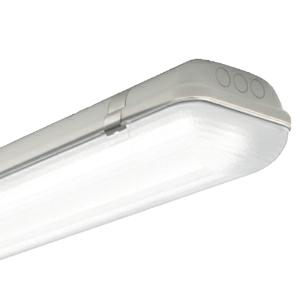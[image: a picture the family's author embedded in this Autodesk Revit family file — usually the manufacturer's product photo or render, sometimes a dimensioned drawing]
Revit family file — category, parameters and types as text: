
# Revit family: 3f_filippi_-_3f_linda_soft_3f_filippi_-_58732_-_3f_linda_led_soft_2x12w_l660
name_source: partatom
category: Lighting Fixtures
units: mm (PartAtom-declared; Revit-internal decimal feet)

## family parameters
Cut with Voids When Loaded = No
Host = Face
Light Source = No
Part Type = Normal
Room Calculation Point = No
Round Connector Dimension = Use Diameter
Shared = No

## types (1)
- 3F Filippi - 3F Linda Soft (1 x LED, 3578 lm, 28 W, 4000 K)
    Apparent Load = 28 VA
    Approval mark = CE
    CIE Flux Codes = 42 72 91 93 100
    Color Rendering = 80
    Color Temperature = 4000 K
    Control Gear = Electronic ballast
    Default Elevation = 1800 mm
    Description = ILLUMINOTECHNICAL
Luminous efficiency 100% (DLOR 93%, ULOR 7%).
Initial luminous flux of the luminaire 3578 lm.
Direct symmetric distribution.
Installation Interdistance Transv.D = 1.35 x hu - Long.D = 1.24 x hu.
Tabular UGR (CIE 117 - 4H-8H; S=0.25H; 70/50/20): RUG 24.4 - 22.3.
Beam angle: 131° - 111°.
Luminous efficacy 128 lm/W.
Lifetime (L93/B10): 30000 h. (tq+25°C)
Lifetime (L90/B10): 50000 h. (tq+25°C)
Lifetime (L85/B10): 80000 h. (tq+25°C)
Lifetime (L80/B10): 100000 h. (tq+25°C)
Lifetime (L85/B10): 50000 h. (tq+35°C)
Sudden decreased luminous flux after 50000 hours: 0% (C0).
Photobiological safety in compliance with IEC/TR 62778: RG0 risk exempt, (IEC 62471).
In compliance with IEC/EN 62722-2-1 - IEC/EN 62717 standards.

SOURCE
2 linear LED modules 12W/840.
Energy efficiency class (UE 2019/2020 - UE 2019/2015): D.
CIE 13.3 Colour rendering index: CRI >80 (R9 <50%).
IES TM-30 Fidelity Index: Rf = 84 Rg = 95.
CCT nominal colour temperature 4000 K.
Colour initial tolerance (MacAdam): SDCM 3.

MECHANICAL
Self-extinguishing V2 polycarbonate housing, injection moulded, RAL 7035 grey.
Ecologic anti-aging injected sealing gasket.
Soft opal diffuser in self-extinguishing V2 polycarbonate, photo-engraved interior, UV stabilised, injection moulded.
Gear-holder reflector in hot-dip galvanised steel, painted with white polyester base.
Snug fit safety snap-lock clips for diffuser mounting in stainless steel, screwdriver opening.
Fixing brackets in stainless steel.
Possibility for technicians to access the interior of the luminaire.
Luminaire with limited surface temperature. - D - (EN 60598-2-24)
Dimensions: 660x160 mm, height 100 mm. Weight 1.65 kg.
IP66 protection degree.
Mechanical strength to impacts IK10 (20 joule).
Glow-wire test resistance 850°C.

ELECTRICAL
Halogen Free electronic wiring 230V-50/60Hz, power factor 0.90, THD <25%, constant output current, SELV, class I, 1 driver.
Power of the luminaire 28 W.
ENEC - CE.
SAFE FLICKER: PstLM=<1 and SVM=<0.4 (IEC TR 61547-1 and IEC TR 63158), to ensure a more comfortable and safe light.
Luminaire compliant with EN 60598-2-22 for power supply from a centralised emergency system CPSS (Central Power Supply System), not incorporated in the luminaire - high risk areas excluded. The default power and flux are 100% in AC and 100% in DC.
Ambient temperature from -20°C to +35°C.
Temperature class T6 max 85°C.
Relative humidity UR: <85%.

INSTALLATION
Ceiling / Suspended / Wall.
All accessories dedicated to this product are available on the Catalog and on our website www.3F-Filippi.com.

APPLICATIONS
Suitable product for food production plants (HACCP), IFS (Food Version 6), BRC (GSFS Food Version 7).
Dry, dusty indoor environments, subject to occasional water splashes.
Luminaires designed for diffuse direct/indirect lighting suitable to provide optimum visual comfort.
Transit areas, stairwells.
Virtually shatterproof polycarbonate compatibly with the fumes / atmospheres that compromise the elasticity of plastic materials.
Suitable for illumination of public car parks and parking grounds referred to DIN 67528:2018-04.

WARNING
Fixture not suitable for cold stores with an ambient temperature <0°C and/or relative humidity >85%.
Luminaire designed for disposal/recycling at end-of-life.
Replaceable (LED only) light source by a professional. Replaceable control gear by a professional.
    Height = 100 mm  [stored 0.328084 ft]
    Lamp = 1 x LED
    Lamp Light Flux = 3578 lm
    Lamp Power = 28 W
    Lamp count = 1
    Length = 660 mm
    Lifetime = 50000 h
    Luminous efficacy = 128 lm/W
    Manufacturer = 3F Filippi
    ModVariant = No
    Model = 3F Filippi - 58732 - 3F Linda LED Soft 2x12W L660
    Mounting Place = Ceiling
    Mounting Type = Pendant
    Number of Poles = 1
    OnlyDefault = Yes
    Power Factor = 1
    Product Name = 3F Filippi - 3F Linda Soft
    Product group = pendant luminaire
    ProductGroupID = 9
    Protection Class = Protection class I
    Protection Degree = IP 66
    RLX_Detail_Level = 1
    RLX_Emergency_Light_Flux = 0 lm
    RLX_Emergency_Type = 0
    RLX_Emergency_Type_DB = No
    RlxData = <blob elided: 69265 chars, md5=5b45bd41>
    Socket = socket
    Standby Power = 0 W
    System Light Flux = 3578 lm
    System Power = 28 W
    Type Comments = Product without accessories
    Type Image = 3ffilippi_3f_linda_led_soft_2x.jpg
    URL = http://relux.com
    VarID = ---
    Voltage = 0 V
    Weight = 0.00 kg
    Width = 160 mm

note: [stored X ft] marks values corroborated as IEEE doubles in the binary element streams (Revit-internal decimal feet)

## geometry (parser evidence)
native form markers: Blend x4, Sweep x14
no freeform markers — native parametric forms only
